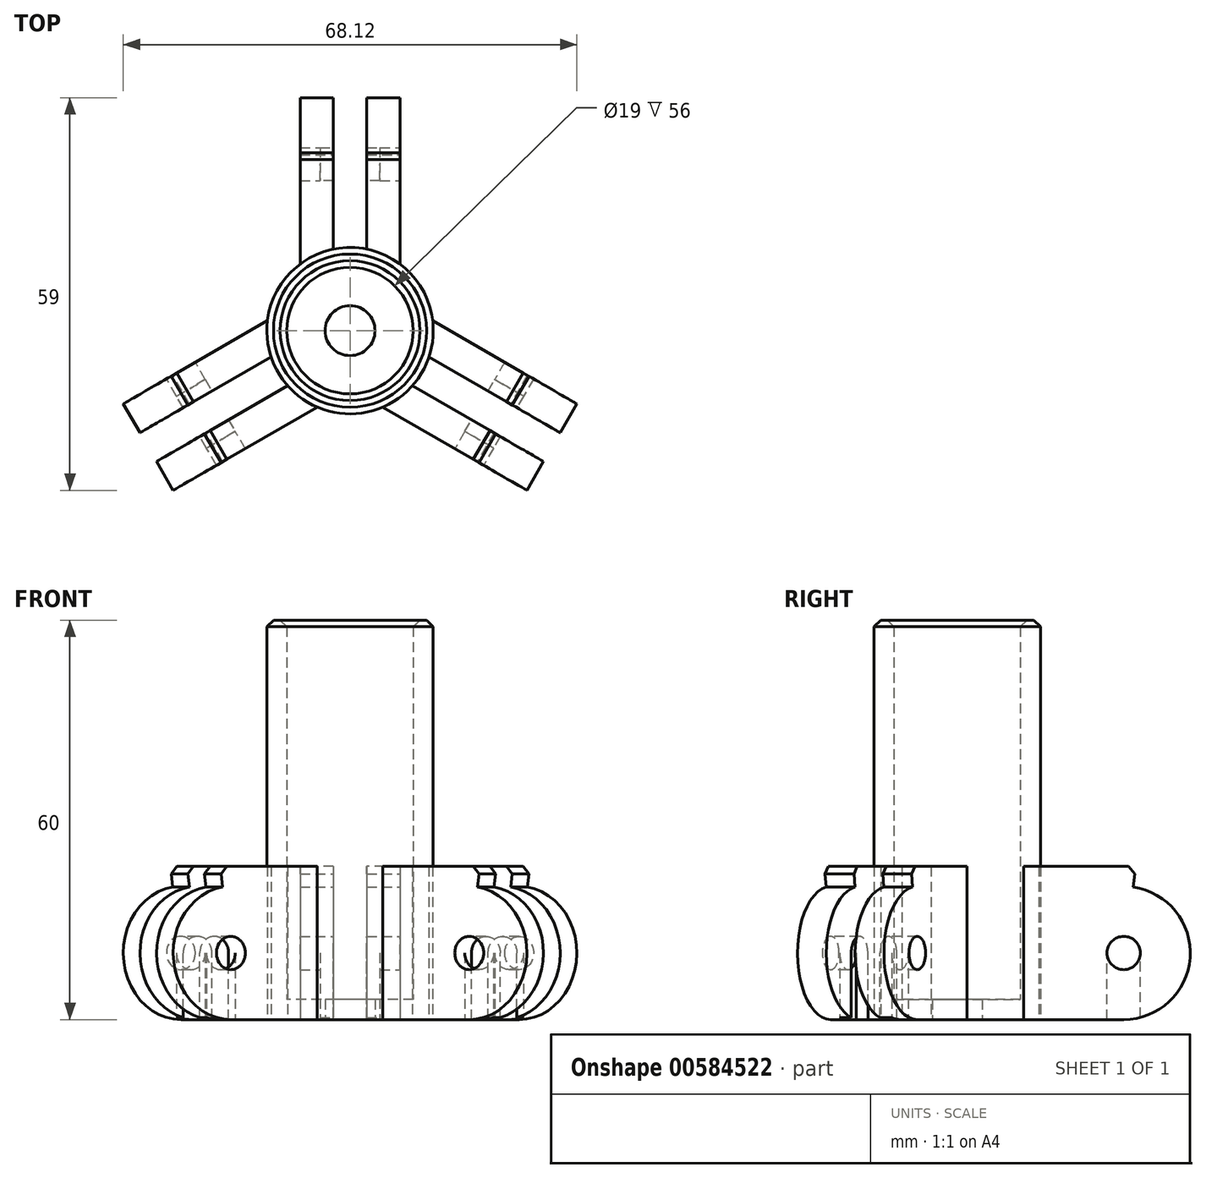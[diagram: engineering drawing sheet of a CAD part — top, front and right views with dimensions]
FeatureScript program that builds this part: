
annotation { "Feature Type Name" : "Feature", "Feature Type Description" : "" }
export const myFeature = defineFeature(function(context is Context, id is Id, definition is map)
    precondition{}
    {
        {
            var Q0;
            Q0=qCreatedBy(makeId("Top.planeOp"),FACE);
            var sketch = newSketch(context, id + "F0", { "sketchPlane" : qUnion([Q0])});
            skCircle(sketch, "E0", {"center": v(0, 0) * mm, "radius": 9.5 * mm});
            skCircle(sketch, "E1", {"center": v(0, 0) * mm, "radius": 12.5 * mm});
            skCircle(sketch, "E2", {"center": v(0, 0) * mm, "radius": 3.75 * mm});
            skSolve(sketch);
        }
        {
            var Q0;
            Q0=makeQuery(id+"F0.imprint","IMPRINT",FACE,{"disambiguationData":[TD([[makeQuery(id+"F0.imprint","IMPRINT",EDGE,{"derivedFrom":sQuery(id+"F0.wireOp",EDGE,"E0")}),-1.0]])]});
            var Q1;
            Q1=makeQuery(id+"F0.imprint","IMPRINT",FACE,{"disambiguationData":[TD([[makeQuery(id+"F0.imprint","IMPRINT",EDGE,{"derivedFrom":sQuery(id+"F0.wireOp",EDGE,"E0")}),1.0]])]});
            extrude(context, id + "F1", {"entities" : qUnion([Q0, Q1]), "depth" : 3 * mm, "offsetDistance" : 25 * mm});
        }
        {
            var Q0;
            Q0 = qSketchRegion(id + "F0", true);
            extrude(context, id + "F2", {"entities" : qUnion([Q0]), "operationType" : NewBodyOperationType.ADD, "depth" : 60 * mm, "offsetDistance" : 25 * mm});
        }
        {
            var Q0;
            Q0=qCreatedBy(makeId("Top.planeOp"),FACE);
            var sketch = newSketch(context, id + "F3", { "sketchPlane" : qUnion([Q0])});
            skLineSegment(sketch, "E3", {"start": v(0, 0) * mm, "end": v(0, 72.36) * mm, "construction": true});
            skLineSegment(sketch, "E4", {"start": v(0, 0) * mm, "end": v(76.55, -44.2) * mm, "construction": true});
            skLineSegment(sketch, "E5", {"start": v(0, 0) * mm, "end": v(-67.46, -38.95) * mm, "construction": true});
            skLineSegment(sketch, "E6.bottom", {"start": v(-7.5, 10) * mm, "end": v(-2.5, 10) * mm});
            skLineSegment(sketch, "E6.top", {"start": v(-7.5, 35) * mm, "end": v(-2.5, 35) * mm});
            skLineSegment(sketch, "E6.left", {"start": v(-7.5, 10) * mm, "end": v(-7.5, 35) * mm});
            skLineSegment(sketch, "E6.right", {"start": v(-2.5, 10) * mm, "end": v(-2.5, 35) * mm});
            skLineSegment(sketch, "E7.MirrorCS", {"start": v(2.5, 10) * mm, "end": v(2.5, 35) * mm});
            skLineSegment(sketch, "E8.MirrorCS", {"start": v(7.5, 10) * mm, "end": v(2.5, 10) * mm});
            skLineSegment(sketch, "E9.MirrorCS", {"start": v(7.5, 35) * mm, "end": v(2.5, 35) * mm});
            skLineSegment(sketch, "E10.MirrorCS", {"start": v(7.5, 10) * mm, "end": v(7.5, 35) * mm});
            skLineSegment(sketch, "E11.MirrorCS", {"start": v(4.91, -11.5) * mm, "end": v(26.56, -24) * mm});
            skLineSegment(sketch, "E12.MirrorCS", {"start": v(7.41, -7.17) * mm, "end": v(29.06, -19.67) * mm});
            skLineSegment(sketch, "E13.MirrorCS", {"start": v(4.91, -11.5) * mm, "end": v(7.41, -7.17) * mm});
            skLineSegment(sketch, "E14.MirrorCS", {"start": v(26.56, -24) * mm, "end": v(29.06, -19.67) * mm});
            skLineSegment(sketch, "E15.MirrorCS", {"start": v(9.91, -2.83) * mm, "end": v(31.56, -15.33) * mm});
            skLineSegment(sketch, "E16.MirrorCS", {"start": v(12.41, 1.5) * mm, "end": v(34.06, -11) * mm});
            skLineSegment(sketch, "E17.MirrorCS", {"start": v(12.41, 1.5) * mm, "end": v(9.91, -2.83) * mm});
            skLineSegment(sketch, "E18.MirrorCS", {"start": v(34.06, -11) * mm, "end": v(31.56, -15.33) * mm});
            skLineSegment(sketch, "E19.MirrorCS", {"start": v(-7.41, -7.17) * mm, "end": v(-29.06, -19.67) * mm});
            skLineSegment(sketch, "E20.MirrorCS", {"start": v(-4.91, -11.5) * mm, "end": v(-7.41, -7.17) * mm});
            skLineSegment(sketch, "E21.MirrorCS", {"start": v(-4.91, -11.5) * mm, "end": v(-26.56, -24) * mm});
            skLineSegment(sketch, "E22.MirrorCS", {"start": v(-26.56, -24) * mm, "end": v(-29.06, -19.67) * mm});
            skLineSegment(sketch, "E23.MirrorCS", {"start": v(-9.91, -2.83) * mm, "end": v(-31.56, -15.33) * mm});
            skLineSegment(sketch, "E24.MirrorCS", {"start": v(-12.41, 1.5) * mm, "end": v(-34.06, -11) * mm});
            skLineSegment(sketch, "E25.MirrorCS", {"start": v(-34.06, -11) * mm, "end": v(-31.56, -15.33) * mm});
            skLineSegment(sketch, "E26.MirrorCS", {"start": v(-12.41, 1.5) * mm, "end": v(-9.91, -2.83) * mm});
            skSolve(sketch);
        }
        {
            var Q0;
            Q0 = qSketchRegion(id + "F3", true);
            extrude(context, id + "F4", {"entities" : qUnion([Q0]), "operationType" : NewBodyOperationType.ADD, "depth" : 23 * mm, "offsetDistance" : 25 * mm});
        }
        {
            var Q0;
            Q0=qCreatedBy(makeId("Right.planeOp"),FACE);
            var sketch = newSketch(context, id + "F5", { "sketchPlane" : qUnion([Q0])});
            skLineSegment(sketch, "E27", {"start": v(0, 0) * mm, "end": v(0, 26.84) * mm, "construction": true});
            skLineSegment(sketch, "E28", {"start": v(0, 0) * mm, "end": v(46.63, 0) * mm, "construction": true});
            skArc(sketch, "E29", {"start": v(25, 0) * mm, "mid": v(34.97, 9.3) * mm, "end": v(26.41, 19.9) * mm});
            skLineSegment(sketch, "E30", {"start": v(37, 24) * mm, "end": v(37, 0) * mm});
            skLineSegment(sketch, "E31", {"start": v(37, 0) * mm, "end": v(25, 0) * mm});
            skCircle(sketch, "E32", {"center": v(25, 10) * mm, "radius": 2.5 * mm});
            skLineSegment(sketch, "E33", {"start": v(26.41, 19.9) * mm, "end": v(27, 24) * mm});
            skLineSegment(sketch, "E34", {"start": v(27, 24) * mm, "end": v(37, 24) * mm});
            skSolve(sketch);
        }
        {
            var Q0;
            Q0 = qSketchRegion(id + "F5", true);
            extrude(context, id + "F6", {"entities" : qUnion([Q0]), "operationType" : NewBodyOperationType.REMOVE, "endBound" : BoundingType.SYMMETRIC, "oppositeDirection" : true, "depth" : 50 * mm, "offsetDistance" : 25 * mm});
        }
        {
            var Q0;
            Q0=makeQuery(id+"F4.opExtrude","SWEPT_FACE",FACE,{"disambiguationData":[OSD([sQuery(id+"F3.wireOp",EDGE,"E15.MirrorCS")])]});
            cPlane(context, id + "F7", {"entities" : qUnion([Q0]), "cplaneType" : CPlaneType.OFFSET, "offset" : 25 * mm, "width" : 150 * mm, "height" : 150 * mm});
        }
        {
            var Q0;
            Q0=qCreatedBy(id+"F7.planeOp",FACE);
            var sketch = newSketch(context, id + "F8", { "sketchPlane" : qUnion([Q0])});
            skLineSegment(sketch, "E35", {"start": v(0, 0) * mm, "end": v(0, 26.55) * mm, "construction": true});
            skLineSegment(sketch, "E36", {"start": v(0, 0) * mm, "end": v(43.8, 0) * mm, "construction": true});
            skArc(sketch, "E37", {"start": v(25, 0) * mm, "mid": v(34.97, 9.3) * mm, "end": v(26.41, 19.9) * mm});
            skLineSegment(sketch, "E38", {"start": v(37, 24) * mm, "end": v(37, 0) * mm});
            skLineSegment(sketch, "E39", {"start": v(37, 0) * mm, "end": v(25, 0) * mm});
            skCircle(sketch, "E40", {"center": v(25, 10) * mm, "radius": 2.5 * mm});
            skLineSegment(sketch, "E41", {"start": v(26.41, 19.9) * mm, "end": v(27, 24) * mm});
            skLineSegment(sketch, "E42", {"start": v(27, 24) * mm, "end": v(37, 24) * mm});
            skSolve(sketch);
        }
        {
            var Q0;
            Q0 = qSketchRegion(id + "F8", true);
            extrude(context, id + "F9", {"entities" : qUnion([Q0]), "operationType" : NewBodyOperationType.REMOVE, "oppositeDirection" : true, "depth" : 50 * mm, "offsetDistance" : 25 * mm});
        }
        {
            var Q0;
            Q0=makeQuery(id+"F4.opExtrude","SWEPT_FACE",FACE,{"disambiguationData":[OSD([sQuery(id+"F3.wireOp",EDGE,"E19.MirrorCS")])]});
            cPlane(context, id + "F10", {"entities" : qUnion([Q0]), "cplaneType" : CPlaneType.OFFSET, "offset" : 25 * mm, "width" : 150 * mm, "height" : 150 * mm});
        }
        {
            var Q0;
            Q0=qCreatedBy(id+"F10.planeOp",FACE);
            var sketch = newSketch(context, id + "F11", { "sketchPlane" : qUnion([Q0])});
            skLineSegment(sketch, "E43", {"start": v(0, 0) * mm, "end": v(0, 26.55) * mm, "construction": true});
            skLineSegment(sketch, "E44", {"start": v(0, 0) * mm, "end": v(43.8, 0) * mm, "construction": true});
            skArc(sketch, "E45", {"start": v(25, 0) * mm, "mid": v(34.97, 9.3) * mm, "end": v(26.41, 19.9) * mm});
            skLineSegment(sketch, "E46", {"start": v(37, 24) * mm, "end": v(37, 0) * mm});
            skLineSegment(sketch, "E47", {"start": v(37, 0) * mm, "end": v(25, 0) * mm});
            skCircle(sketch, "E48", {"center": v(25, 10) * mm, "radius": 2.5 * mm});
            skLineSegment(sketch, "E49", {"start": v(26.41, 19.9) * mm, "end": v(27, 24) * mm});
            skLineSegment(sketch, "E50", {"start": v(27, 24) * mm, "end": v(37, 24) * mm});
            skSolve(sketch);
        }
        {
            var Q0;
            Q0 = qSketchRegion(id + "F11", true);
            extrude(context, id + "F12", {"entities" : qUnion([Q0]), "operationType" : NewBodyOperationType.REMOVE, "oppositeDirection" : true, "depth" : 50 * mm, "offsetDistance" : 25 * mm});
        }
        {
            var Q0;
            Q0=makeQuery(id+"F12.boolean.opBoolean","INTERSECT",EDGE,{"derivedFrom":[makeQuery(id+"F4.opExtrude","CAP_FACE",FACE,{"disambiguationData":[OSD([sQuery(id+"F3.wireOp",EDGE,"E23.MirrorCS"),sQuery(id+"F3.wireOp",EDGE,"E24.MirrorCS"),sQuery(id+"F3.wireOp",EDGE,"E25.MirrorCS"),sQuery(id+"F3.wireOp",EDGE,"E26.MirrorCS")])],"isStart":false}),makeQuery(id+"F12.opExtrude","SWEPT_FACE",FACE,{"disambiguationData":[OSD([sQuery(id+"F11.wireOp",EDGE,"E49")])]})]});
            var Q1;
            Q1=makeQuery(id+"F12.boolean.opBoolean","INTERSECT",EDGE,{"derivedFrom":[makeQuery(id+"F4.opExtrude","CAP_FACE",FACE,{"disambiguationData":[OSD([sQuery(id+"F3.wireOp",EDGE,"E20.MirrorCS"),sQuery(id+"F3.wireOp",EDGE,"E21.MirrorCS"),sQuery(id+"F3.wireOp",EDGE,"E19.MirrorCS"),sQuery(id+"F3.wireOp",EDGE,"E22.MirrorCS")])],"isStart":false}),makeQuery(id+"F12.opExtrude","SWEPT_FACE",FACE,{"disambiguationData":[OSD([sQuery(id+"F11.wireOp",EDGE,"E49")])]})]});
            var Q2;
            Q2=makeQuery(id+"F9.boolean.opBoolean","INTERSECT",EDGE,{"derivedFrom":[makeQuery(id+"F4.opExtrude","CAP_FACE",FACE,{"disambiguationData":[OSD([sQuery(id+"F3.wireOp",EDGE,"E11.MirrorCS"),sQuery(id+"F3.wireOp",EDGE,"E12.MirrorCS"),sQuery(id+"F3.wireOp",EDGE,"E13.MirrorCS"),sQuery(id+"F3.wireOp",EDGE,"E14.MirrorCS")])],"isStart":false}),makeQuery(id+"F9.opExtrude","SWEPT_FACE",FACE,{"disambiguationData":[OSD([sQuery(id+"F8.wireOp",EDGE,"E41")])]})]});
            var Q3;
            Q3=makeQuery(id+"F9.boolean.opBoolean","INTERSECT",EDGE,{"derivedFrom":[makeQuery(id+"F4.opExtrude","CAP_FACE",FACE,{"disambiguationData":[OSD([sQuery(id+"F3.wireOp",EDGE,"E15.MirrorCS"),sQuery(id+"F3.wireOp",EDGE,"E16.MirrorCS"),sQuery(id+"F3.wireOp",EDGE,"E17.MirrorCS"),sQuery(id+"F3.wireOp",EDGE,"E18.MirrorCS")])],"isStart":false}),makeQuery(id+"F9.opExtrude","SWEPT_FACE",FACE,{"disambiguationData":[OSD([sQuery(id+"F8.wireOp",EDGE,"E41")])]})]});
            var Q4;
            Q4=makeQuery(id+"F6.boolean.opBoolean","INTERSECT",EDGE,{"derivedFrom":[makeQuery(id+"F4.opExtrude","CAP_FACE",FACE,{"disambiguationData":[OSD([sQuery(id+"F3.wireOp",EDGE,"E7.MirrorCS"),sQuery(id+"F3.wireOp",EDGE,"E8.MirrorCS"),sQuery(id+"F3.wireOp",EDGE,"E9.MirrorCS"),sQuery(id+"F3.wireOp",EDGE,"E10.MirrorCS")])],"isStart":false}),makeQuery(id+"F6.opExtrude","SWEPT_FACE",FACE,{"disambiguationData":[OSD([sQuery(id+"F5.wireOp",EDGE,"E33")])]})]});
            var Q5;
            Q5=makeQuery(id+"F6.boolean.opBoolean","INTERSECT",EDGE,{"derivedFrom":[makeQuery(id+"F4.opExtrude","CAP_FACE",FACE,{"disambiguationData":[OSD([sQuery(id+"F3.wireOp",EDGE,"E6.bottom"),sQuery(id+"F3.wireOp",EDGE,"E6.top"),sQuery(id+"F3.wireOp",EDGE,"E6.left"),sQuery(id+"F3.wireOp",EDGE,"E6.right")])],"isStart":false}),makeQuery(id+"F6.opExtrude","SWEPT_FACE",FACE,{"disambiguationData":[OSD([sQuery(id+"F5.wireOp",EDGE,"E33")])]})]});
            var Q6;
            Q6=makeQuery(id+"F2.opExtrude","CAP_EDGE",EDGE,{"disambiguationData":[OSD([sQuery(id+"F0.wireOp",EDGE,"E0")])],"isStart":false});
            var Q7;
            Q7=makeQuery(id+"F2.opExtrude","CAP_EDGE",EDGE,{"disambiguationData":[OSD([sQuery(id+"F0.wireOp",EDGE,"E1")])],"isStart":false});
            chamfer(context, id + "F13", {"entities" : qUnion([Q0, Q1, Q2, Q3, Q4, Q5, Q6, Q7]), "width" : 1 * mm, "tangentPropagation" : true});
        }
        {
            var Q0;
            Q0=qCreatedBy(makeId("Top.planeOp"),FACE);
            var sketch = newSketch(context, id + "F14", { "sketchPlane" : qUnion([Q0])});
            skLineSegment(sketch, "E51", {"start": v(0, 22.5) * mm, "end": v(-4.5, 22.5) * mm});
            skLineSegment(sketch, "E52", {"start": v(-4.5, 22.5) * mm, "end": v(-4.5, 27.5) * mm});
            skLineSegment(sketch, "E53", {"start": v(-4.5, 27.5) * mm, "end": v(0, 27.5) * mm});
            skLineSegment(sketch, "E54.MirrorCS", {"start": v(0, 22.5) * mm, "end": v(4.5, 22.5) * mm});
            skLineSegment(sketch, "E55.MirrorCS", {"start": v(4.5, 22.5) * mm, "end": v(4.5, 27.5) * mm});
            skLineSegment(sketch, "E56.MirrorCS", {"start": v(4.5, 27.5) * mm, "end": v(0, 27.5) * mm});
            skLineSegment(sketch, "E57.MirrorCS", {"start": v(-19.49, -11.25) * mm, "end": v(-17.24, -15.15) * mm});
            skLineSegment(sketch, "E58.MirrorCS", {"start": v(-19.49, -11.25) * mm, "end": v(-21.74, -7.35) * mm});
            skLineSegment(sketch, "E59.MirrorCS", {"start": v(-21.74, -7.35) * mm, "end": v(-26.07, -9.85) * mm});
            skLineSegment(sketch, "E60.MirrorCS", {"start": v(-26.07, -9.85) * mm, "end": v(-23.82, -13.75) * mm});
            skLineSegment(sketch, "E61.MirrorCS", {"start": v(-21.57, -17.65) * mm, "end": v(-23.82, -13.75) * mm});
            skLineSegment(sketch, "E62.MirrorCS", {"start": v(-17.24, -15.15) * mm, "end": v(-21.57, -17.65) * mm});
            skLineSegment(sketch, "E63.MirrorCS", {"start": v(19.49, -11.25) * mm, "end": v(17.24, -15.15) * mm});
            skLineSegment(sketch, "E64.MirrorCS", {"start": v(19.49, -11.25) * mm, "end": v(21.74, -7.35) * mm});
            skLineSegment(sketch, "E65.MirrorCS", {"start": v(26.07, -9.85) * mm, "end": v(23.82, -13.75) * mm});
            skLineSegment(sketch, "E66.MirrorCS", {"start": v(21.57, -17.65) * mm, "end": v(23.82, -13.75) * mm});
            skLineSegment(sketch, "E67.MirrorCS", {"start": v(17.24, -15.15) * mm, "end": v(21.57, -17.65) * mm});
            skLineSegment(sketch, "E68.MirrorCS", {"start": v(21.74, -7.35) * mm, "end": v(26.07, -9.85) * mm});
            skSolve(sketch);
        }
        {
            var Q0;
            Q0 = qSketchRegion(id + "F14", true);
            extrude(context, id + "F15", {"entities" : qUnion([Q0]), "operationType" : NewBodyOperationType.REMOVE, "depth" : 10 * mm, "offsetDistance" : 25 * mm});
        }
    });
